# Revit family: MRID-6
name_source: partatom
category: Lighting Fixtures
units: mm (PartAtom-declared; Revit-internal decimal feet)

## family parameters
Always vertical = Yes
Cut with Voids When Loaded = No
Host = Ceiling
Light Source = Yes
Maintain Annotation Orientation = No
OmniClass Number = 23.80.70.11
OmniClass Title = Luminaries for Internal Lighting
Part Type = Normal
Room Calculation Point = No
Round Connector Dimension = Use Diameter
Shared = No

## types (10) — shared parameters
Assembly Code = D5020200
Color Filter = 16777215
Default Elevation = 0' - 0"
Description = LED Non-Ferrous MRI 6in Downlight Luminaire
Dimming Lamp Color Temperature Shift = <None>
Emit Shape Visible in Rendering = No
Emit from Circle Diameter = 2' - 0"
Housing Finish = Metal - Viscor - White
Lamp = LED
Length = 0' - 9 17/32"
Lens Finish = Polycarbonate - Viscor - Frosted Round
Manufacturer = CERTOLUX A DIVISION OF VISCOR
Model = MRID
Tilt Angle = 90.00°
URL = https://viscor.com
Voltage = 120 V
Width = 0' - 9 21/32"

## per-type parameters (varying)
| type | Apparent Load | Lamp Wattage | Photometric Web File |
| MRID6-RSL-MW-WD-840K020LUNV | 21 VA | 21 VA | MRID6-RSL-MW-WD-840K020LUNV.ies |
| MRID6-RSL-MW-WD-840K030LUNV | 31 VA | 31 VA | MRID6-RSL-MW-WD-840K030LUNV.ies |
| MRID6-RSL-MW-WD-840K035LUNV | 36 VA | 36 VA | MRID6-RSL-MW-WD-840K035LUNV.ies |
| MRID6-RSL-PL-WD-840K020LUNV | 21 VA | 21 VA | MRID6-RSL-PL-WD-840K020LUNV.ies |
| MRID6-RSL-PL-WD-840K030LUNV | 31 VA | 31 VA | MRID6-RSL-PL-WD-840K030LUNV.ies |
| MRID6-RSL-PL-WD-840K035LUNV | 36 VA | 36 VA | MRID6-RSL-PL-WD-840K035LUNV.ies |
| MRID6-RSL-SS-MED-840K025LUNV | 26 VA | 26 VA | MRID6-RSL-SS-MED-840K025LUNV.ies |
| MRID6-RSL-SS-MED-840K035LUNV | 36 VA | 36 VA | MRID6-RSL-SS-MED-840K035LUNV.ies |
| MRID6-RSL-SS-WD-840K025LUNV | 26 VA | 26 VA | MRID6-RSL-SS-WD-840K025LUNV.ies |
| MRID6-RSL-SS-WD-840K035LUNV | 36 VA | 36 VA | MRID6-RSL-SS-WD-840K035LUNV.ies |

## geometry (parser evidence)
native form markers: Sweep x2
no freeform markers — native parametric forms only
